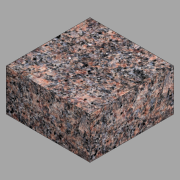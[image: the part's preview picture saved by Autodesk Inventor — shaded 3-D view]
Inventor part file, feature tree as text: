
AUTODESK INVENTOR PART (.ipt)
format: ipt  version: 2022.2 (Build 262287000, 287)  size: 139,776 bytes
history: native  units: in
note: dims shown in document units (in); Inventor stores cm internally (conversion verified against a paired STEP export)
features: extrude x1, sketch x1
ambient origin geometry x8: Origin, YZ Plane, XZ Plane, XY Plane, X Axis, Y Axis, Z Axis, Center Point
bodies: Solid1 (feature_tree)
feature tree (2):
  extrude  "Extrusion1"  Depth=4.0in
  sketch  "Sketch1"  dims[d0=4.0in d1=4.0in d2=2.0in d3=0.0in]
